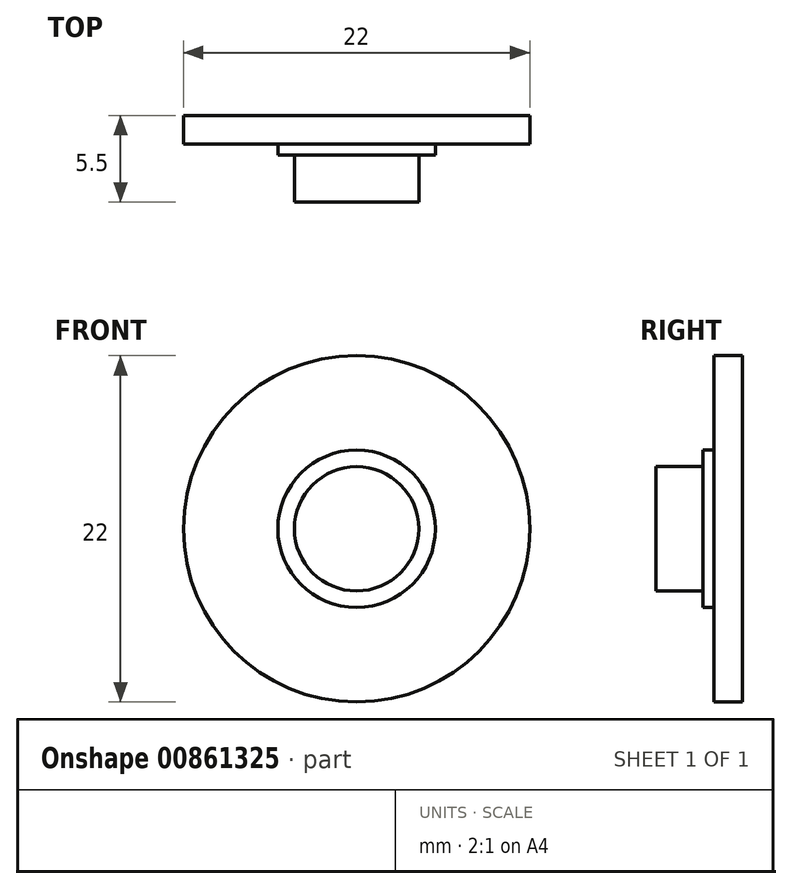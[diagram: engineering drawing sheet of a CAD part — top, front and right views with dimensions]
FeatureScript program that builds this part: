
annotation { "Feature Type Name" : "Feature", "Feature Type Description" : "" }
export const myFeature = defineFeature(function(context is Context, id is Id, definition is map)
    precondition{}
    {
        {
            var Q0;
            Q0=qCreatedBy(makeId("Front.planeOp"),FACE);
            var sketch = newSketch(context, id + "F0", { "sketchPlane" : qUnion([Q0])});
            skCircle(sketch, "E0", {"center": v(0, 0) * mm, "radius": 11 * mm});
            skSolve(sketch);
        }
        {
            var Q0;
            Q0=makeQuery(id+"F0.imprint","IMPRINT",FACE,{"disambiguationData":[TD([[makeQuery(id+"F0.imprint","IMPRINT",EDGE,{"derivedFrom":sQuery(id+"F0.wireOp",EDGE,"E0")}),1.0]])]});
            extrude(context, id + "F1", {"entities" : qUnion([Q0]), "depth" : 1.8 * mm, "offsetDistance" : 25 * mm});
        }
        {
            var Q0;
            Q0=qCreatedBy(makeId("Front.planeOp"),FACE);
            var sketch = newSketch(context, id + "F2", { "sketchPlane" : qUnion([Q0])});
            skCircle(sketch, "E1", {"center": v(0, 0) * mm, "radius": 3.95 * mm});
            skSolve(sketch);
        }
        {
            var Q0;
            Q0 = qSketchRegion(id + "F2", true);
            extrude(context, id + "F3", {"entities" : qUnion([Q0]), "operationType" : NewBodyOperationType.ADD, "depth" : 5.5 * mm, "offsetDistance" : 25 * mm});
        }
        {
            var Q0;
            Q0=qCreatedBy(makeId("Front.planeOp"),FACE);
            var sketch = newSketch(context, id + "F4", { "sketchPlane" : qUnion([Q0])});
            skCircle(sketch, "E2", {"center": v(0, 0) * mm, "radius": 5 * mm});
            skSolve(sketch);
        }
        {
            var Q0;
            Q0 = qSketchRegion(id + "F4", true);
            extrude(context, id + "F5", {"entities" : qUnion([Q0]), "operationType" : NewBodyOperationType.ADD, "depth" : 2.5 * mm, "offsetDistance" : 25 * mm});
        }
    });
